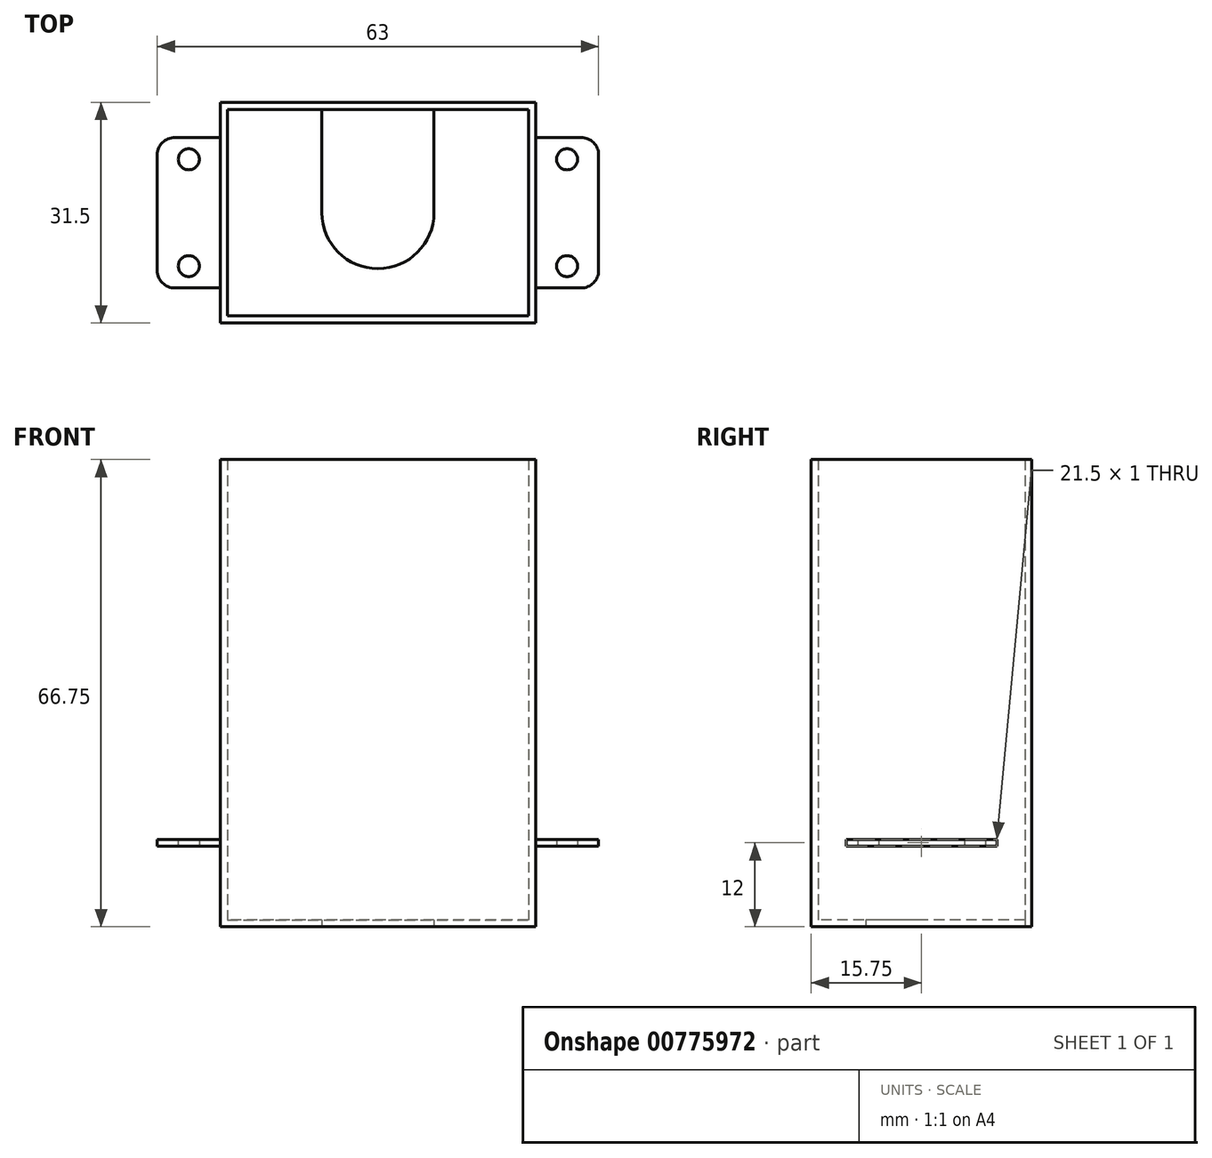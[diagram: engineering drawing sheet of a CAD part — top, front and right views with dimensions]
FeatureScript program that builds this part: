
annotation { "Feature Type Name" : "Feature", "Feature Type Description" : "" }
export const myFeature = defineFeature(function(context is Context, id is Id, definition is map)
    precondition{}
    {
        {
            var Q0;
            Q0=qCreatedBy(makeId("Top.planeOp"),FACE);
            var sketch = newSketch(context, id + "F0", { "sketchPlane" : qUnion([Q0])});
            skCircle(sketch, "E0", {"center": v(-27, -7.62) * mm, "radius": 1.5 * mm});
            skCircle(sketch, "E1", {"center": v(-27, 7.62) * mm, "radius": 1.5 * mm});
            skCircle(sketch, "E2", {"center": v(27, -7.62) * mm, "radius": 1.5 * mm});
            skCircle(sketch, "E3", {"center": v(27, 7.62) * mm, "radius": 1.5 * mm});
            skLineSegment(sketch, "E4", {"start": v(-27, 7.62) * mm, "end": v(-27, -7.62) * mm, "construction": true});
            skLineSegment(sketch, "E5", {"start": v(27, -7.62) * mm, "end": v(27, 7.62) * mm, "construction": true});
            skLineSegment(sketch, "E6", {"start": v(-31.5, 8.25) * mm, "end": v(-31.5, -8.25) * mm});
            skLineSegment(sketch, "E7", {"start": v(-29, -10.75) * mm, "end": v(-22.5, -10.75) * mm});
            skLineSegment(sketch, "E8", {"start": v(-22.5, -10.75) * mm, "end": v(-22.5, 10.75) * mm});
            skLineSegment(sketch, "E9", {"start": v(-22.5, 10.75) * mm, "end": v(-29, 10.75) * mm});
            skLineSegment(sketch, "E10", {"start": v(-27, 0) * mm, "end": v(27, 0) * mm, "construction": true});
            skLineSegment(sketch, "E11.MirrorCS", {"start": v(22.5, -10.75) * mm, "end": v(22.5, 10.75) * mm});
            skLineSegment(sketch, "E12.MirrorCS", {"start": v(22.5, 10.75) * mm, "end": v(29, 10.75) * mm});
            skLineSegment(sketch, "E13.MirrorCS", {"start": v(31.5, 8.25) * mm, "end": v(31.5, -8.25) * mm});
            skLineSegment(sketch, "E14.MirrorCS", {"start": v(29, -10.75) * mm, "end": v(22.5, -10.75) * mm});
            skLineSegment(sketch, "E15", {"start": v(-22.5, 10.75) * mm, "end": v(22.5, 10.75) * mm});
            skLineSegment(sketch, "E16", {"start": v(22.5, -10.75) * mm, "end": v(-22.5, -10.75) * mm});
            skPoint(sketch, "E17.visualSharp", {"position": v(-31.5, -10.75) * mm});
            skArc(sketch, "E17.filletArc", {"start": v(-31.5, -8.25) * mm, "mid": v(-30.77, -10.02) * mm, "end": v(-29, -10.75) * mm});
            skPoint(sketch, "E18.visualSharp", {"position": v(-31.5, 10.75) * mm});
            skArc(sketch, "E18.filletArc", {"start": v(-29, 10.75) * mm, "mid": v(-30.77, 10.02) * mm, "end": v(-31.5, 8.25) * mm});
            skPoint(sketch, "E19.visualSharp", {"position": v(31.5, 10.75) * mm});
            skArc(sketch, "E19.filletArc", {"start": v(31.5, 8.25) * mm, "mid": v(30.77, 10.02) * mm, "end": v(29, 10.75) * mm});
            skPoint(sketch, "E20.visualSharp", {"position": v(31.5, -10.75) * mm});
            skArc(sketch, "E20.filletArc", {"start": v(29, -10.75) * mm, "mid": v(30.77, -10.02) * mm, "end": v(31.5, -8.25) * mm});
            skSolve(sketch);
        }
        {
            var Q0;
            Q0=makeQuery(id+"F0.imprint","IMPRINT",FACE,{"disambiguationData":[TD([[makeQuery(id+"F0.imprint","IMPRINT",EDGE,{"derivedFrom":sQuery(id+"F0.wireOp",EDGE,"E0")}),-1.0]])]});
            var Q1;
            Q1=makeQuery(id+"F0.imprint","IMPRINT",FACE,{"disambiguationData":[TD([[makeQuery(id+"F0.imprint","IMPRINT",EDGE,{"derivedFrom":sQuery(id+"F0.wireOp",EDGE,"E2")}),-1.0]])]});
            extrude(context, id + "F1", {"entities" : qUnion([Q0, Q1]), "depth" : 1 * mm, "offsetDistance" : 25 * mm});
        }
        {
            var Q0;
            Q0=makeQuery(id+"F1.opExtrude","CAP_FACE",FACE,{"disambiguationData":[OSD([sQuery(id+"F0.wireOp",EDGE,"E0"),sQuery(id+"F0.wireOp",EDGE,"E1"),sQuery(id+"F0.wireOp",EDGE,"E6"),sQuery(id+"F0.wireOp",EDGE,"E7"),sQuery(id+"F0.wireOp",EDGE,"E8"),sQuery(id+"F0.wireOp",EDGE,"E9")])],"isStart":true});
            cPlane(context, id + "F2", {"entities" : qUnion([Q0]), "cplaneType" : CPlaneType.OFFSET, "offset" : 11.5 * mm, "width" : 150 * mm, "height" : 150 * mm});
        }
        {
            var Q0;
            Q0=qCreatedBy(id+"F2.planeOp",FACE);
            var sketch = newSketch(context, id + "F3", { "sketchPlane" : qUnion([Q0])});
            skLineSegment(sketch, "E21.0.0", {"start": v(-22.5, -10.75) * mm, "end": v(-22.5, 10.75) * mm});
            skLineSegment(sketch, "E21.0.1", {"start": v(-22.5, 10.75) * mm, "end": v(-29, 10.75) * mm, "construction": true});
            skArc(sketch, "E21.0.2", {"start": v(-29, 10.75) * mm, "mid": v(-30.77, 10.02) * mm, "end": v(-31.5, 8.25) * mm, "construction": true});
            skLineSegment(sketch, "E21.0.3", {"start": v(-31.5, 8.25) * mm, "end": v(-31.5, -8.25) * mm, "construction": true});
            skArc(sketch, "E21.0.4", {"start": v(-31.5, -8.25) * mm, "mid": v(-30.77, -10.02) * mm, "end": v(-29, -10.75) * mm, "construction": true});
            skLineSegment(sketch, "E21.0.5", {"start": v(-29, -10.75) * mm, "end": v(-22.5, -10.75) * mm, "construction": true});
            skLineSegment(sketch, "E22.0.0", {"start": v(22.5, -10.75) * mm, "end": v(29, -10.75) * mm, "construction": true});
            skArc(sketch, "E22.0.1", {"start": v(29, -10.75) * mm, "mid": v(30.77, -10.02) * mm, "end": v(31.5, -8.25) * mm, "construction": true});
            skLineSegment(sketch, "E22.0.2", {"start": v(31.5, -8.25) * mm, "end": v(31.5, 8.25) * mm, "construction": true});
            skArc(sketch, "E22.0.3", {"start": v(31.5, 8.25) * mm, "mid": v(30.77, 10.02) * mm, "end": v(29, 10.75) * mm, "construction": true});
            skLineSegment(sketch, "E22.0.4", {"start": v(29, 10.75) * mm, "end": v(22.5, 10.75) * mm, "construction": true});
            skLineSegment(sketch, "E22.0.5", {"start": v(22.5, 10.75) * mm, "end": v(22.5, -10.75) * mm});
            skLineSegment(sketch, "E23", {"start": v(-22.5, 10.75) * mm, "end": v(-22.5, 15.75) * mm});
            skLineSegment(sketch, "E24", {"start": v(-22.5, 15.75) * mm, "end": v(22.5, 15.75) * mm});
            skLineSegment(sketch, "E25", {"start": v(22.5, 15.75) * mm, "end": v(22.5, 10.75) * mm});
            skLineSegment(sketch, "E26", {"start": v(22.5, -10.75) * mm, "end": v(22.5, -15.75) * mm});
            skLineSegment(sketch, "E27", {"start": v(22.5, -15.75) * mm, "end": v(-22.5, -15.75) * mm});
            skLineSegment(sketch, "E28", {"start": v(-22.5, -15.75) * mm, "end": v(-22.5, -10.75) * mm});
            skLineSegment(sketch, "E29.0", {"start": v(-21.5, -10.75) * mm, "end": v(-21.5, 10.75) * mm});
            skLineSegment(sketch, "E29.1", {"start": v(-21.5, -14.75) * mm, "end": v(-21.5, -10.75) * mm});
            skLineSegment(sketch, "E29.2", {"start": v(-21.5, 10.75) * mm, "end": v(-21.5, 14.75) * mm});
            skLineSegment(sketch, "E29.3", {"start": v(21.5, -14.75) * mm, "end": v(-21.5, -14.75) * mm});
            skLineSegment(sketch, "E29.4", {"start": v(-21.5, 14.75) * mm, "end": v(21.5, 14.75) * mm});
            skLineSegment(sketch, "E29.5", {"start": v(21.5, 14.75) * mm, "end": v(21.5, 10.75) * mm});
            skLineSegment(sketch, "E29.6", {"start": v(21.5, 10.75) * mm, "end": v(21.5, -10.75) * mm});
            skLineSegment(sketch, "E29.7", {"start": v(21.5, -10.75) * mm, "end": v(21.5, -14.75) * mm});
            skLineSegment(sketch, "E30", {"start": v(-8, -14.75) * mm, "end": v(-8, 0) * mm});
            skLineSegment(sketch, "E31", {"start": v(8, -14.75) * mm, "end": v(8, 0) * mm});
            skArc(sketch, "E32", {"start": v(8, 0) * mm, "mid": v(0, 8) * mm, "end": v(-8, 0) * mm});
            skSolve(sketch);
        }
        {
            var Q0;
            Q0=makeQuery(id+"F3.imprint","IMPRINT",FACE,{"disambiguationData":[TD([[makeQuery(id+"F3.imprint","IMPRINT",EDGE,{"derivedFrom":sQuery(id+"F3.wireOp",EDGE,"E21.0.0")}),-1.0]])]});
            extrude(context, id + "F4", {"entities" : qUnion([Q0]), "operationType" : NewBodyOperationType.ADD, "oppositeDirection" : true, "depth" : 66.75 * mm, "offsetDistance" : 25 * mm});
        }
        {
            var Q0;
            Q0=makeQuery(id+"F3.imprint","IMPRINT",FACE,{"disambiguationData":[TD([[makeQuery(id+"F3.imprint","IMPRINT",EDGE,{"derivedFrom":sQuery(id+"F3.wireOp",EDGE,"E29.0")}),-1.0]])]});
            extrude(context, id + "F5", {"entities" : qUnion([Q0]), "operationType" : NewBodyOperationType.ADD, "oppositeDirection" : true, "depth" : 1 * mm, "offsetDistance" : 25 * mm});
        }
    });
